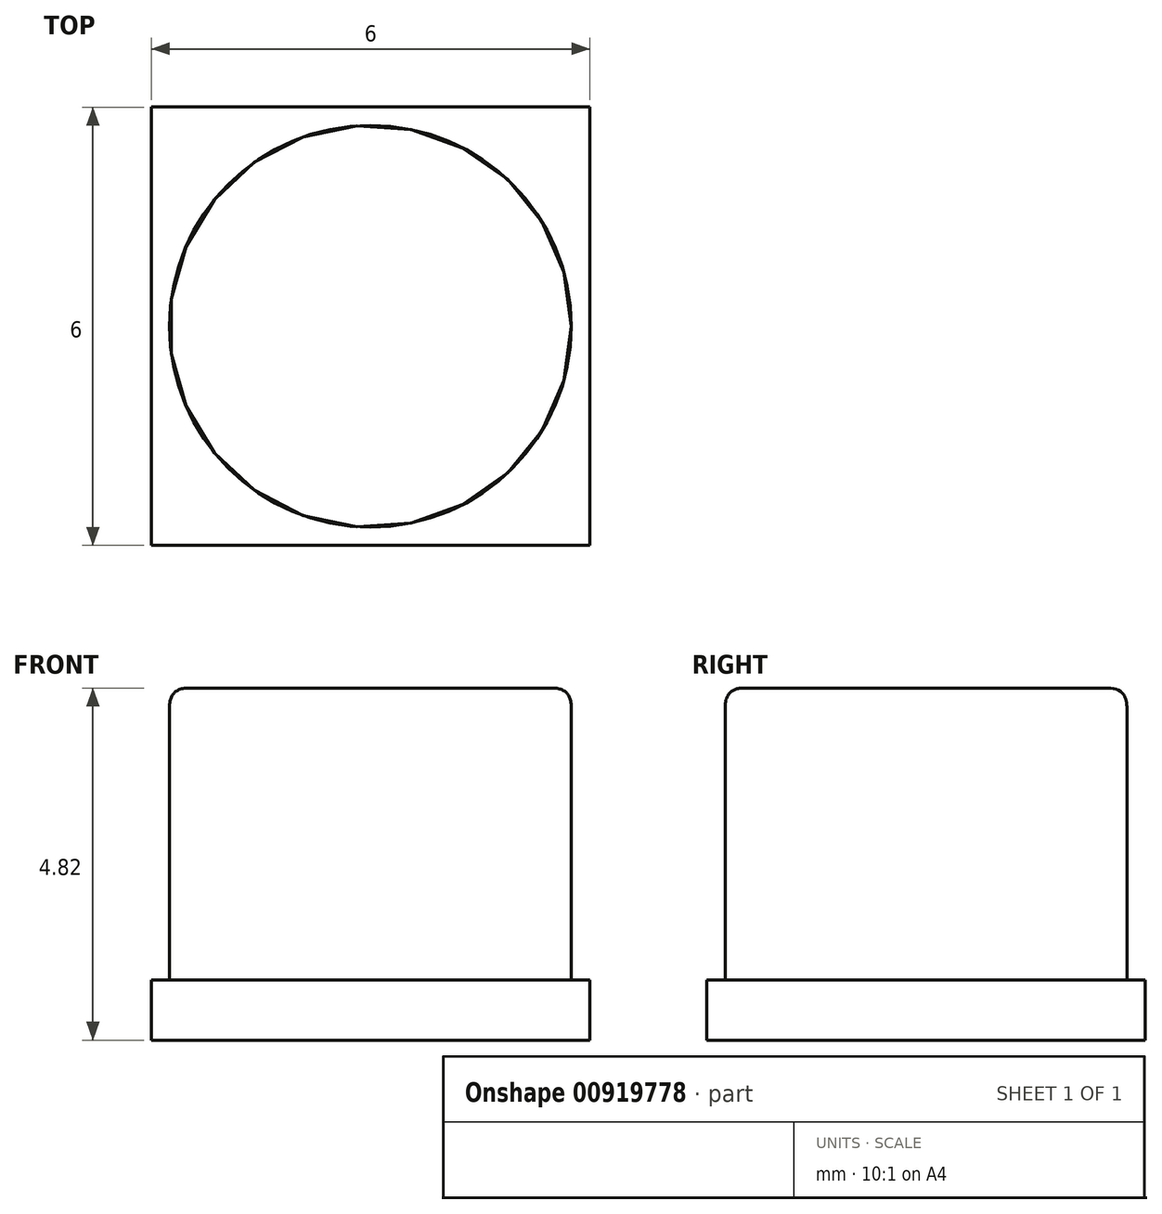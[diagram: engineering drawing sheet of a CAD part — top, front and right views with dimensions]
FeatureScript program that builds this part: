
annotation { "Feature Type Name" : "Feature", "Feature Type Description" : "" }
export const myFeature = defineFeature(function(context is Context, id is Id, definition is map)
    precondition{}
    {
        {
            var Q0;
            Q0=qCreatedBy(makeId("Top.planeOp"),FACE);
            var sketch = newSketch(context, id + "F0", { "sketchPlane" : qUnion([Q0])});
            skLineSegment(sketch, "E0.bottom", {"start": v(-3.61, -7.1) * mm, "end": v(2.39, -7.1) * mm});
            skLineSegment(sketch, "E0.top", {"start": v(-3.61, -13.1) * mm, "end": v(2.39, -13.1) * mm});
            skLineSegment(sketch, "E0.left", {"start": v(-3.61, -7.1) * mm, "end": v(-3.61, -13.1) * mm});
            skLineSegment(sketch, "E0.right", {"start": v(2.39, -7.1) * mm, "end": v(2.39, -13.1) * mm});
            skSolve(sketch);
        }
        {
            var Q0;
            Q0=qSketchRegion(id+"F0",true);
            extrude(context, id + "F1", {"entities" : qUnion([Q0]), "depth" : .82 * mm, "offsetDistance" : 25 * mm});
        }
        {
            var Q0;
            Q0=makeQuery(id+"F1.opExtrude","CAP_FACE",FACE,{"disambiguationData":[OSD([sQuery(id+"F0.wireOp",EDGE,"E0.bottom"),sQuery(id+"F0.wireOp",EDGE,"E0.top"),sQuery(id+"F0.wireOp",EDGE,"E0.left"),sQuery(id+"F0.wireOp",EDGE,"E0.right")])],"isStart":false});
            var sketch = newSketch(context, id + "F2", { "sketchPlane" : qUnion([Q0])});
            skCircle(sketch, "E1", {"center": v(-0.61, -10.1) * mm, "radius": 2.75 * mm});
            skPoint(sketch, "E1.centerSnap0", {"position": v(-0.61, -7.1) * mm});
            skPoint(sketch, "E1.centerSnap1", {"position": v(2.39, -10.1) * mm});
            skSolve(sketch);
        }
        {
            var Q0;
            Q0=makeQuery(id+"F2.imprint","IMPRINT",FACE,{"disambiguationData":[TD([[makeQuery(id+"F2.imprint","IMPRINT",EDGE,{"derivedFrom":sQuery(id+"F2.wireOp",EDGE,"E1")}),1.0]])]});
            extrude(context, id + "F3", {"entities" : qUnion([Q0]), "operationType" : NewBodyOperationType.ADD, "depth" : 4 * mm, "offsetDistance" : 25 * mm});
        }
        {
            var Q0;
            Q0=makeQuery(id+"F1.opExtrude","CAP_FACE",FACE,{"disambiguationData":[OSD([sQuery(id+"F0.wireOp",EDGE,"E0.bottom"),sQuery(id+"F0.wireOp",EDGE,"E0.top"),sQuery(id+"F0.wireOp",EDGE,"E0.left"),sQuery(id+"F0.wireOp",EDGE,"E0.right")])],"isStart":false});
            var sketch = newSketch(context, id + "F4", { "sketchPlane" : qUnion([Q0])});
            skPoint(sketch, "E2.startSnap0", {"position": v(-3.61, -10.1) * mm});
            skPoint(sketch, "E2.startSnap1", {"position": v(-0.61, -13.1) * mm});
            skArc(sketch, "E3", {"start": v(-0.61, -8.35) * mm, "mid": v(-2.36, -10.1) * mm, "end": v(-0.61, -11.85) * mm});
            skLineSegment(sketch, "E4", {"start": v(-0.61, -11.85) * mm, "end": v(-0.61, -8.35) * mm});
            skSolve(sketch);
        }
        {
            var Q0;
            Q0=makeQuery(id+"F3.opExtrude","CAP_EDGE",EDGE,{"disambiguationData":[OSD([sQuery(id+"F2.wireOp",EDGE,"E1")])],"isStart":false});
            fillet(context, id + "F5", {"entities" : qUnion([Q0]), "radius" : 0.27 * mm, "rho" : .5, "crossSection" : FilletCrossSection.CONIC, "allowEdgeOverflow" : false});
        }
    });
